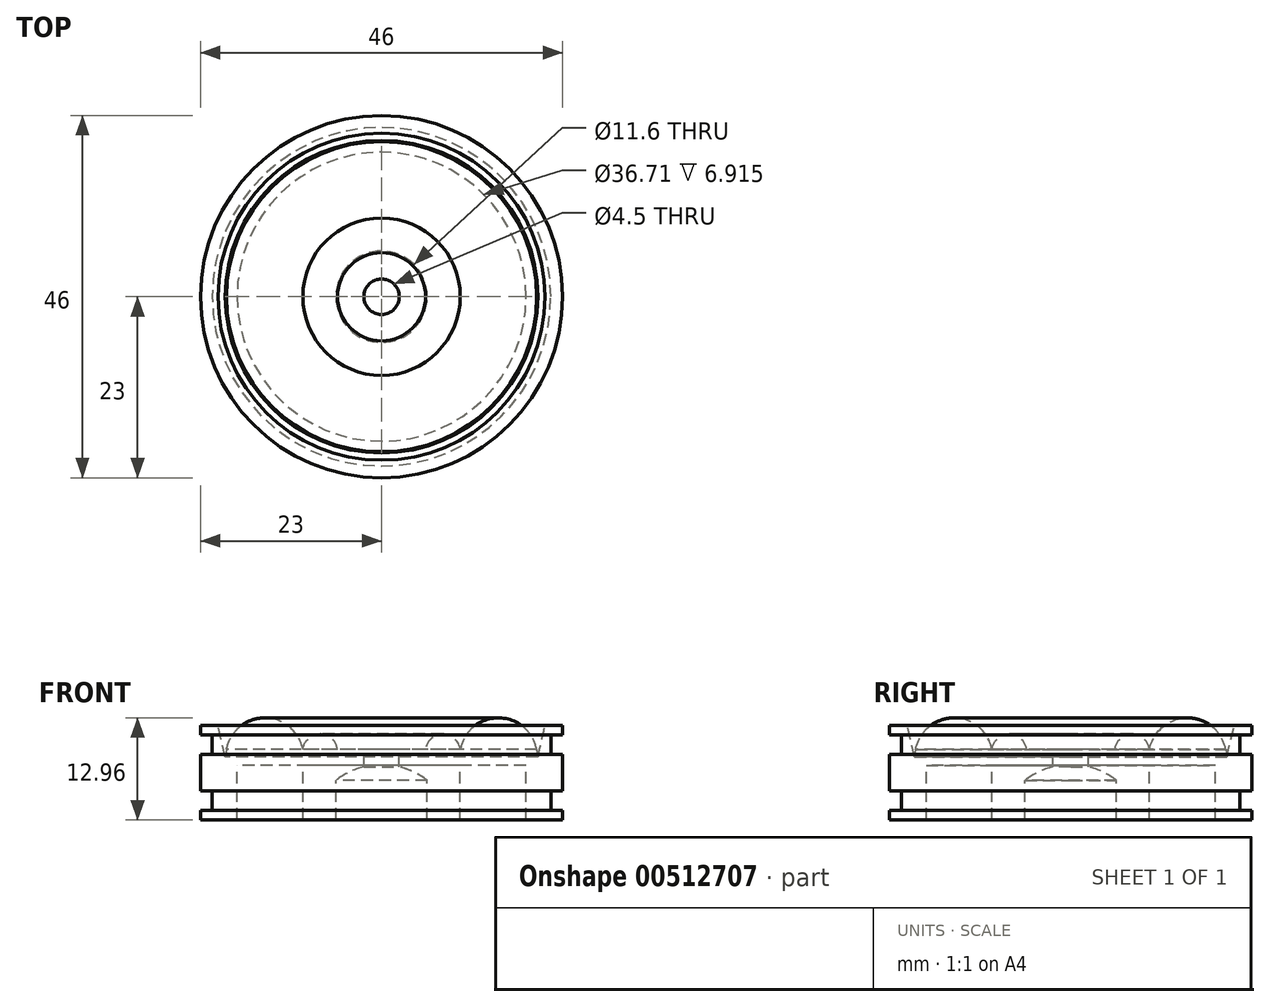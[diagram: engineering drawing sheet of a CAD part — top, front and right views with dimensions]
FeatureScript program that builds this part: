
annotation { "Feature Type Name" : "Feature", "Feature Type Description" : "" }
export const myFeature = defineFeature(function(context is Context, id is Id, definition is map)
    precondition{}
    {
        {
            var Q0;
            Q0=qCreatedBy(makeId("Front.planeOp"),FACE);
            var sketch = newSketch(context, id + "F0", { "sketchPlane" : qUnion([Q0])});
            skLineSegment(sketch, "E0", {"start": v(0, 0) * mm, "end": v(4.85, 0) * mm});
            skLineSegment(sketch, "E1", {"start": v(5.8, -8.92) * mm, "end": v(10, -8.92) * mm});
            skLineSegment(sketch, "E2", {"start": v(10, -8.92) * mm, "end": v(10, -2) * mm});
            skLineSegment(sketch, "E3", {"start": v(18.36, -8.92) * mm, "end": v(18.36, -2) * mm});
            skLineSegment(sketch, "E4", {"start": v(20.77, 3.08) * mm, "end": v(23, 3.08) * mm});
            skLineSegment(sketch, "E5", {"start": v(23, 3.08) * mm, "end": v(23, 1.88) * mm});
            skLineSegment(sketch, "E6", {"start": v(23, -8.92) * mm, "end": v(18.36, -8.92) * mm});
            skLineSegment(sketch, "E7", {"start": v(0, 0) * mm, "end": v(0, -1.92) * mm});
            skLineSegment(sketch, "E8", {"start": v(23, 1.88) * mm, "end": v(21.5, 1.88) * mm});
            skLineSegment(sketch, "E9", {"start": v(21.5, 1.88) * mm, "end": v(21.5, -0.62) * mm});
            skLineSegment(sketch, "E10", {"start": v(21.5, -0.62) * mm, "end": v(23, -0.62) * mm});
            skLineSegment(sketch, "E11", {"start": v(23, -7.72) * mm, "end": v(21.5, -7.72) * mm});
            skLineSegment(sketch, "E12", {"start": v(21.5, -7.72) * mm, "end": v(21.5, -5.22) * mm});
            skLineSegment(sketch, "E13", {"start": v(21.5, -5.22) * mm, "end": v(23, -5.22) * mm});
            skLineSegment(sketch, "E14.trimOffspring", {"start": v(23, -0.62) * mm, "end": v(23, -5.22) * mm});
            skLineSegment(sketch, "E15.trimOffspring", {"start": v(23, -7.72) * mm, "end": v(23, -8.92) * mm});
            skLineSegment(sketch, "E16", {"start": v(10, -2) * mm, "end": v(18.36, -2) * mm});
            skPoint(sketch, "E17.visualSharp", {"position": v(18.36, 0) * mm});
            skPoint(sketch, "E18.orphan", {"position": v(10, 0) * mm});
            skArc(sketch, "E19", {"start": v(10, 0) * mm, "mid": v(7.8, 1.97) * mm, "end": v(5.6, 0) * mm});
            skArc(sketch, "E20", {"start": v(19.7, 0) * mm, "mid": v(14.85, 4.04) * mm, "end": v(10, 0) * mm});
            skLineSegment(sketch, "E21", {"start": v(20.77, 3.08) * mm, "end": v(19.85, -0.93) * mm});
            skLineSegment(sketch, "E22", {"start": v(19.85, -0.93) * mm, "end": v(19.7, 0) * mm});
            skLineSegment(sketch, "E23", {"start": v(5.8, -3.92) * mm, "end": v(5.8, -8.92) * mm});
            skPoint(sketch, "E24.orphan", {"position": v(0, -8.92) * mm});
            skPoint(sketch, "E25.visualSharp", {"position": v(5.8, -1.92) * mm});
            skLineSegment(sketch, "E26", {"start": v(4.85, 0) * mm, "end": v(5.6, 0) * mm});
            skArc(sketch, "E27", {"start": v(5.8, -3.92) * mm, "mid": v(3.07, -2.43) * mm, "end": v(0, -1.92) * mm});
            skSolve(sketch);
        }
        {
            var Q0;
            Q0=makeQuery(id+"F0.imprint","IMPRINT",FACE,{"disambiguationData":[TD([[makeQuery(id+"F0.imprint","IMPRINT",EDGE,{"derivedFrom":sQuery(id+"F0.wireOp",EDGE,"E0")}),-1.0]])]});
            var Q1;
            Q1=sQuery(id+"F0.wireOp",EDGE,"E7");
            revolve(context, id + "F1", {"entities" : qUnion([Q0]), "axis" : qUnion([Q1]), "revolveType" : RevolveType.FULL});
        }
        {
            var Q0;
            Q0=makeQuery(id+"F1.opRevolve","SWEPT_FACE",FACE,{"disambiguationData":[OSD([sQuery(id+"F0.wireOp",EDGE,"E0")])]});
            var sketch = newSketch(context, id + "F2", { "sketchPlane" : qUnion([Q0])});
            skCircle(sketch, "E28", {"center": v(0, 0) * mm, "radius": 2.25 * mm});
            skSolve(sketch);
        }
        {
            var Q0;
            Q0=makeQuery(id+"F2.imprint","IMPRINT",FACE,{"disambiguationData":[TD([[makeQuery(id+"F2.imprint","IMPRINT",EDGE,{"derivedFrom":sQuery(id+"F2.wireOp",EDGE,"E28")}),1.0]])]});
            extrude(context, id + "F3", {"entities" : qUnion([Q0]), "operationType" : NewBodyOperationType.REMOVE, "endBound" : BoundingType.THROUGH_ALL, "oppositeDirection" : true, "depth" : 25 * mm});
        }
    });
